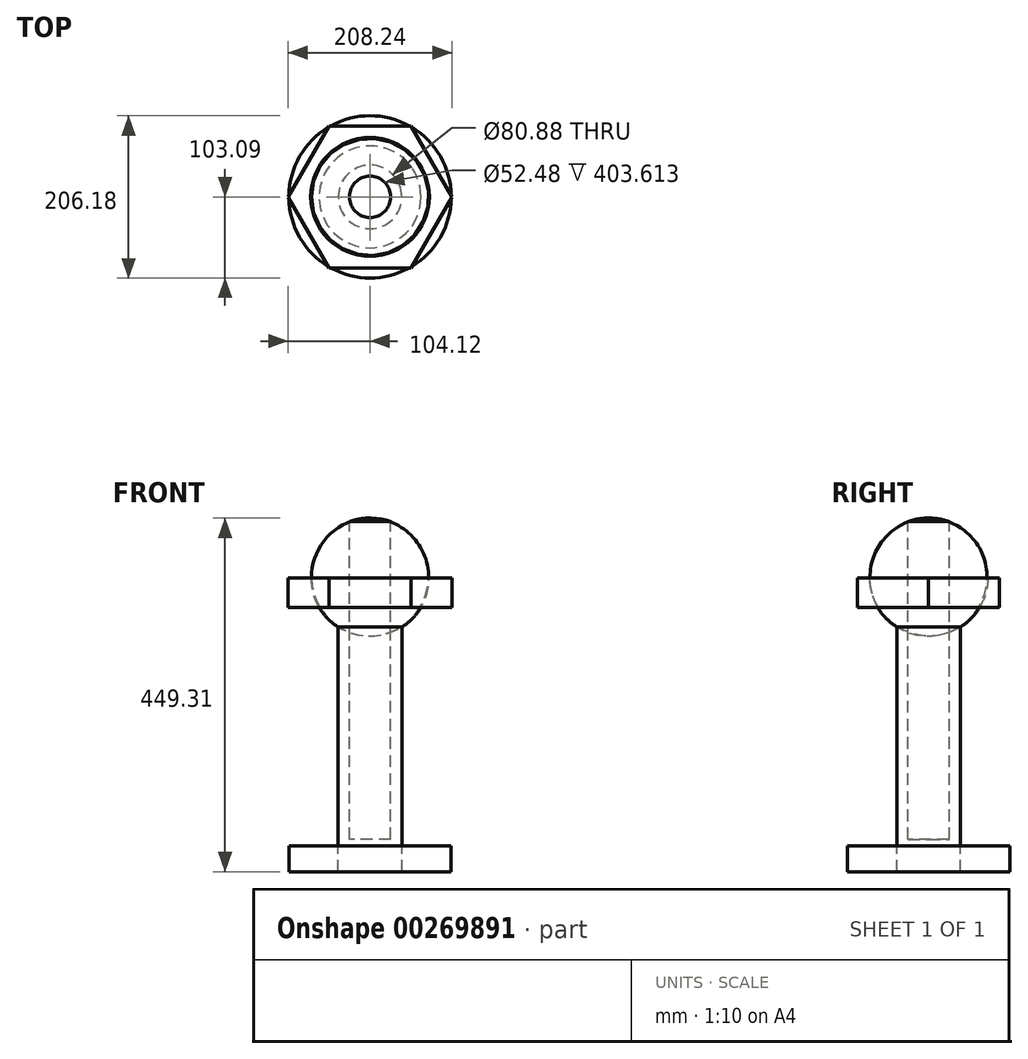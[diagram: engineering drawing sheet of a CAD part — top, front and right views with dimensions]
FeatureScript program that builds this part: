
annotation { "Feature Type Name" : "Feature", "Feature Type Description" : "" }
export const myFeature = defineFeature(function(context is Context, id is Id, definition is map)
    precondition{}
    {
        {
            var Q0;
            Q0=qCreatedBy(makeId("Right.planeOp"),FACE);
            var sketch = newSketch(context, id + "F0", { "sketchPlane" : qUnion([Q0])});
            skArc(sketch, "E0", {"start": v(0, -73.89) * mm, "mid": v(75.44, 1.02) * mm, "end": v(0, 75.93) * mm});
            skLineSegment(sketch, "E1", {"start": v(0, 75.93) * mm, "end": v(0, -73.89) * mm});
            skSolve(sketch);
        }
        {
            var Q0;
            Q0=makeQuery(id+"F0.imprint","IMPRINT",FACE,{"disambiguationData":[TD([[makeQuery(id+"F0.imprint","IMPRINT",EDGE,{"derivedFrom":sQuery(id+"F0.wireOp",EDGE,"E0")}),1.0]])]});
            var Q1;
            Q1=sQuery(id+"F0.wireOp",EDGE,"E1");
            revolve(context, id + "F1", {"entities" : qUnion([Q0]), "axis" : qUnion([Q1]), "revolveType" : RevolveType.FULL});
        }
        {
            var Q0;
            Q0=qCreatedBy(makeId("Top.planeOp"),FACE);
            var sketch = newSketch(context, id + "F2", { "sketchPlane" : qUnion([Q0])});
            skCircle(sketch, "E2", {"center": v(0, 0) * mm, "radius": 40.44 * mm});
            skSolve(sketch);
        }
        {
            var Q0;
            Q0 = qSketchRegion(id + "F2", true);
            var Q1;
            Q1=sQuery(id+"F2.wireOp",EDGE,"E2");
            extrude(context, id + "F3", {"entities" : qUnion([Q0]), "operationType" : NewBodyOperationType.ADD, "surfaceEntities" : qUnion([Q1]), "oppositeDirection" : true, "depth" : 340.36 * mm});
        }
        {
            var Q0;
            Q0=qCreatedBy(makeId("Top.planeOp"),FACE);
            var sketch = newSketch(context, id + "F4", { "sketchPlane" : qUnion([Q0])});
            skCircle(sketch, "E3.cCircle", {"center": v(0, 0) * mm, "radius": 90.17 * mm, "construction": true});
            skLineSegment(sketch, "E3.0", {"start": v(-52.06, 90.17) * mm, "end": v(52.06, 90.17) * mm});
            skLineSegment(sketch, "E3.1", {"start": v(52.06, 90.17) * mm, "end": v(104.12, 0) * mm});
            skLineSegment(sketch, "E3.2", {"start": v(104.12, 0) * mm, "end": v(52.06, -90.17) * mm});
            skLineSegment(sketch, "E3.3", {"start": v(52.06, -90.17) * mm, "end": v(-52.06, -90.17) * mm});
            skLineSegment(sketch, "E3.4", {"start": v(-52.06, -90.17) * mm, "end": v(-104.12, 0) * mm});
            skLineSegment(sketch, "E3.5", {"start": v(-104.12, 0) * mm, "end": v(-52.06, 90.17) * mm});
            skPoint(sketch, "E3.0.midPoint", {"position": v(0, 90.17) * mm});
            skSolve(sketch);
        }
        {
            var Q0;
            Q0 = qSketchRegion(id + "F4", true);
            extrude(context, id + "F5", {"entities" : qUnion([Q0]), "operationType" : NewBodyOperationType.ADD, "oppositeDirection" : true, "depth" : 37.6 * mm});
        }
        {
            var Q0;
            Q0=qCreatedBy(makeId("Top.planeOp"),FACE);
            var sketch = newSketch(context, id + "F6", { "sketchPlane" : qUnion([Q0])});
            skCircle(sketch, "E4", {"center": v(0, 0) * mm, "radius": 26.24 * mm});
            skSolve(sketch);
        }
        {
            var Q0;
            Q0 = qSketchRegion(id + "F6", true);
            extrude(context, id + "F7", {"entities" : qUnion([Q0]), "operationType" : NewBodyOperationType.REMOVE, "oppositeDirection" : true, "depth" : 332.23 * mm});
        }
        {
            var Q0;
            Q0 = qSketchRegion(id + "F6", true);
            extrude(context, id + "F8", {"entities" : qUnion([Q0]), "operationType" : NewBodyOperationType.REMOVE, "depth" : 170.43 * mm});
        }
        {
            var Q0;
            Q0=makeQuery(id+"F3.opExtrude","CAP_FACE",FACE,{"disambiguationData":[OSD([sQuery(id+"F2.wireOp",EDGE,"E2")])],"isStart":false});
            var sketch = newSketch(context, id + "F9", { "sketchPlane" : qUnion([Q0])});
            skCircle(sketch, "E5", {"center": v(0, 0) * mm, "radius": 103.1 * mm});
            skSolve(sketch);
        }
        {
            var Q0;
            Q0=makeQuery(id+"F9.imprint","IMPRINT",FACE,{"disambiguationData":[TD([[makeQuery(id+"F9.imprint","IMPRINT",EDGE,{"derivedFrom":sQuery(id+"F9.wireOp",EDGE,"E5")}),1.0]])]});
            extrude(context, id + "F10", {"entities" : qUnion([Q0]), "depth" : 33.02 * mm});
        }
    });
